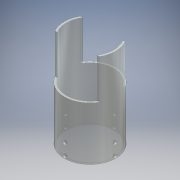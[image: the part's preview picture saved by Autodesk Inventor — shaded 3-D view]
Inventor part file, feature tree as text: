
AUTODESK INVENTOR PART (.ipt)
format: ipt  version: 2016 (Build 200138000, 138)  size: 238,080 bytes
history: native  units: mm
features: sketch x14, hole x8, other x6, extrude x5
ambient origin geometry x8: Origin, YZ Plane, XZ Plane, XY Plane, X Axis, Y Axis, Z Axis, Center Point
bodies: Body1 (feature_tree)
feature tree (33):
  other  "ソリッド1"
  extrude  "押し出し1"  Depth=102.0mm
  sketch  "スケッチ2"
  other  "作業平面1"
  other  "作業平面2"
  other  "作業平面3"
  other  "作業平面4"
  sketch  "スケッチ3"
  sketch  "スケッチ4"
  sketch  "スケッチ5"
  sketch  "スケッチ6"
  other  "作業平面5"
  extrude  "押し出し9"  Depth=110.0mm
  sketch  "スケッチ9"
  extrude  "押し出し12"  TaperAngle=30.0deg  [1 undecoded]
  extrude  "押し出し13"  TaperAngle=150.0deg  [1 undecoded]
  sketch  "スケッチ12"
  sketch  "スケッチ13"
  sketch  "スケッチ14"
  sketch  "スケッチ15"
  extrude  "押し出し18"  Depth=20.0mm TaperAngle=0.0deg
  hole  "穴1"  [1 undecoded]
  hole  "穴2"  [1 undecoded]
  hole  "穴3"  [1 undecoded]
  hole  "穴4"  [1 undecoded]
  hole  "穴5"  [1 undecoded]
  hole  "穴6"  [1 undecoded]
  hole  "穴7"  [1 undecoded]
  hole  "穴8"  [1 undecoded]
  sketch  "スケッチ1"
  sketch  "スケッチ10"
  sketch  "スケッチ11"
  sketch  "スケッチ16"
note: 10 required parameter values undecoded (feature->parameter linkage not recoverable at this tier; creation-order binding heuristic only, values carry confidence <= 0.55)
